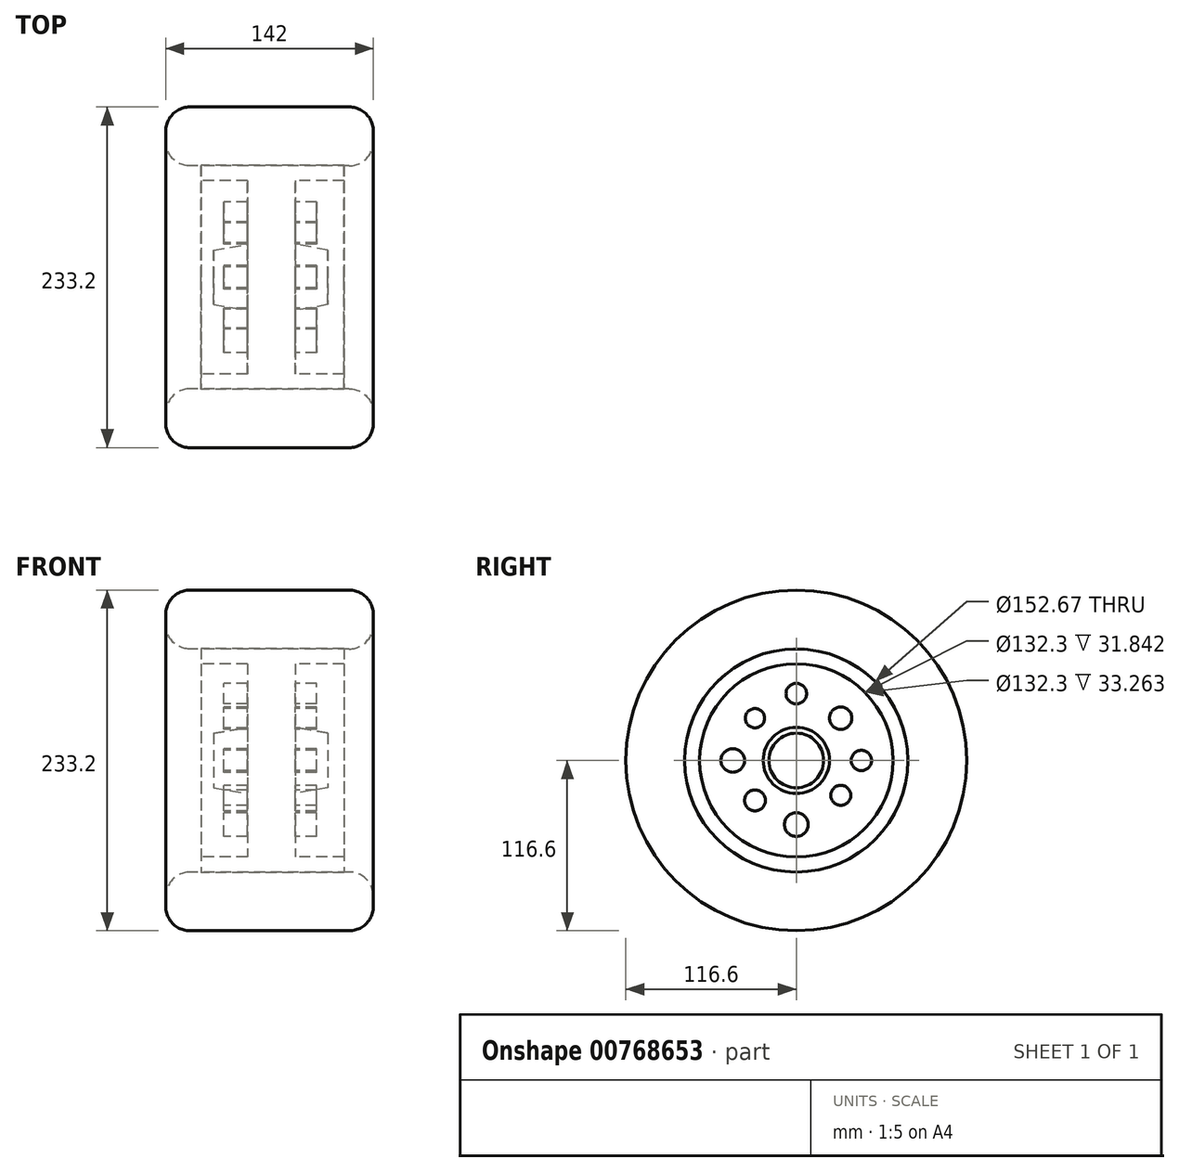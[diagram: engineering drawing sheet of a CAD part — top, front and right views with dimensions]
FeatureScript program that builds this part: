
annotation { "Feature Type Name" : "Feature", "Feature Type Description" : "" }
export const myFeature = defineFeature(function(context is Context, id is Id, definition is map)
    precondition{}
    {
        {
            var Q0;
            Q0=qCreatedBy(makeId("Front.planeOp"),FACE);
            var sketch = newSketch(context, id + "F0", { "sketchPlane" : qUnion([Q0])});
            skLineSegment(sketch, "E0.bottom", {"start": v(-47.39, 76.67) * mm, "end": v(50.41, 76.67) * mm});
            skLineSegment(sketch, "E0.top", {"start": v(-47.39, 66.15) * mm, "end": v(50.41, 66.15) * mm});
            skLineSegment(sketch, "E0.left", {"start": v(-47.39, 76.67) * mm, "end": v(-47.39, 66.15) * mm});
            skLineSegment(sketch, "E0.right", {"start": v(50.41, 76.67) * mm, "end": v(50.41, 66.15) * mm});
            skLineSegment(sketch, "E1.bottom", {"start": v(-15.55, 66.15) * mm, "end": v(17.15, 66.15) * mm});
            skLineSegment(sketch, "E1.top", {"start": v(-15.55, 22.65) * mm, "end": v(17.15, 22.65) * mm});
            skLineSegment(sketch, "E1.left", {"start": v(-15.55, 66.15) * mm, "end": v(-15.55, 22.65) * mm});
            skLineSegment(sketch, "E1.right", {"start": v(17.15, 66.15) * mm, "end": v(17.15, 22.65) * mm});
            skLineSegment(sketch, "E2", {"start": v(-15.55, 22.65) * mm, "end": v(-38.86, 18.67) * mm});
            skLineSegment(sketch, "E3", {"start": v(-38.86, 18.67) * mm, "end": v(-38.86, 0) * mm});
            skLineSegment(sketch, "E4", {"start": v(-38.86, 0) * mm, "end": v(39.32, 0) * mm});
            skLineSegment(sketch, "E5", {"start": v(39.32, 0) * mm, "end": v(39.32, 18.67) * mm});
            skLineSegment(sketch, "E6", {"start": v(39.32, 18.67) * mm, "end": v(17.15, 22.65) * mm});
            skSolve(sketch);
        }
        {
            var Q0;
            Q0=qSketchRegion(id+"F0",true);
            var Q1;
            Q1=sQuery(id+"F0.wireOp",EDGE,"E4");
            revolve(context, id + "F1", {"entities" : qUnion([Q0]), "axis" : qUnion([Q1]), "revolveType" : RevolveType.FULL});
        }
        {
            var Q0;
            Q0=qCreatedBy(makeId("Front.planeOp"),FACE);
            var sketch = newSketch(context, id + "F2", { "sketchPlane" : qUnion([Q0])});
            skLineSegment(sketch, "E7.bottom", {"start": v(-71.46, 116.6) * mm, "end": v(70.54, 116.6) * mm});
            skLineSegment(sketch, "E7.top", {"start": v(-71.46, 76.34) * mm, "end": v(70.54, 76.34) * mm});
            skLineSegment(sketch, "E7.left", {"start": v(-71.46, 116.6) * mm, "end": v(-71.46, 76.34) * mm});
            skLineSegment(sketch, "E7.right", {"start": v(70.54, 116.6) * mm, "end": v(70.54, 76.34) * mm});
            skLineSegment(sketch, "E8", {"start": v(-75.93, 0) * mm, "end": v(87.2, 0) * mm});
            skSolve(sketch);
        }
        {
            var Q0;
            Q0=qSketchRegion(id+"F2",true);
            var Q1;
            Q1=sQuery(id+"F2.wireOp",EDGE,"E8");
            revolve(context, id + "F3", {"entities" : qUnion([Q0]), "axis" : qUnion([Q1]), "revolveType" : RevolveType.FULL});
        }
        {
            var Q0;
            Q0=makeQuery(id+"F3.opRevolve","SWEPT_EDGE",EDGE,{"disambiguationData":[OSD([sQuery(id+"F2.wireOp",EDGE,"E7.bottom"),sQuery(id+"F2.wireOp",EDGE,"E7.left")])]});
            var Q1;
            Q1=makeQuery(id+"F3.opRevolve","SWEPT_EDGE",EDGE,{"disambiguationData":[OSD([sQuery(id+"F2.wireOp",EDGE,"E7.top"),sQuery(id+"F2.wireOp",EDGE,"E7.left")])]});
            var Q2;
            Q2=makeQuery(id+"F3.opRevolve","SWEPT_EDGE",EDGE,{"disambiguationData":[OSD([sQuery(id+"F2.wireOp",EDGE,"E7.bottom"),sQuery(id+"F2.wireOp",EDGE,"E7.right")])]});
            var Q3;
            Q3=makeQuery(id+"F3.opRevolve","SWEPT_EDGE",EDGE,{"disambiguationData":[OSD([sQuery(id+"F2.wireOp",EDGE,"E7.top"),sQuery(id+"F2.wireOp",EDGE,"E7.right")])]});
            fillet(context, id + "F4", {"entities" : qUnion([Q0, Q1, Q2, Q3]), "radius" : 16.56 * mm, "tangentPropagation" : true, "allowEdgeOverflow" : false});
        }
        {
            var Q0;
            Q0=qCreatedBy(makeId("Right.planeOp"),FACE);
            var sketch = newSketch(context, id + "F5", { "sketchPlane" : qUnion([Q0])});
            skCircle(sketch, "E9", {"center": v(-43.48, 0) * mm, "radius": 8.05 * mm});
            skCircle(sketch, "E10", {"center": v(0, 45.74) * mm, "radius": 7.04 * mm});
            skCircle(sketch, "E11", {"center": v(44.54, 0) * mm, "radius": 6.96 * mm});
            skCircle(sketch, "E12", {"center": v(0, -43.88) * mm, "radius": 8.11 * mm});
            skCircle(sketch, "E13", {"center": v(-28.27, 28.94) * mm, "radius": 6.59 * mm});
            skCircle(sketch, "E14", {"center": v(30.4, 28.94) * mm, "radius": 7.64 * mm});
            skCircle(sketch, "E15", {"center": v(30.4, -23.87) * mm, "radius": 6.86 * mm});
            skCircle(sketch, "E16", {"center": v(-28.27, -27.34) * mm, "radius": 7.16 * mm});
            skSolve(sketch);
        }
        {
            var Q0;
            Q0=qSketchRegion(id+"F5",true);
            extrude(context, id + "F6", {"entities" : qUnion([Q0]), "operationType" : NewBodyOperationType.ADD, "endBound" : BoundingType.SYMMETRIC, "depth" : 63.5 * mm, "offsetDistance" : 25.4 * mm});
        }
    });
